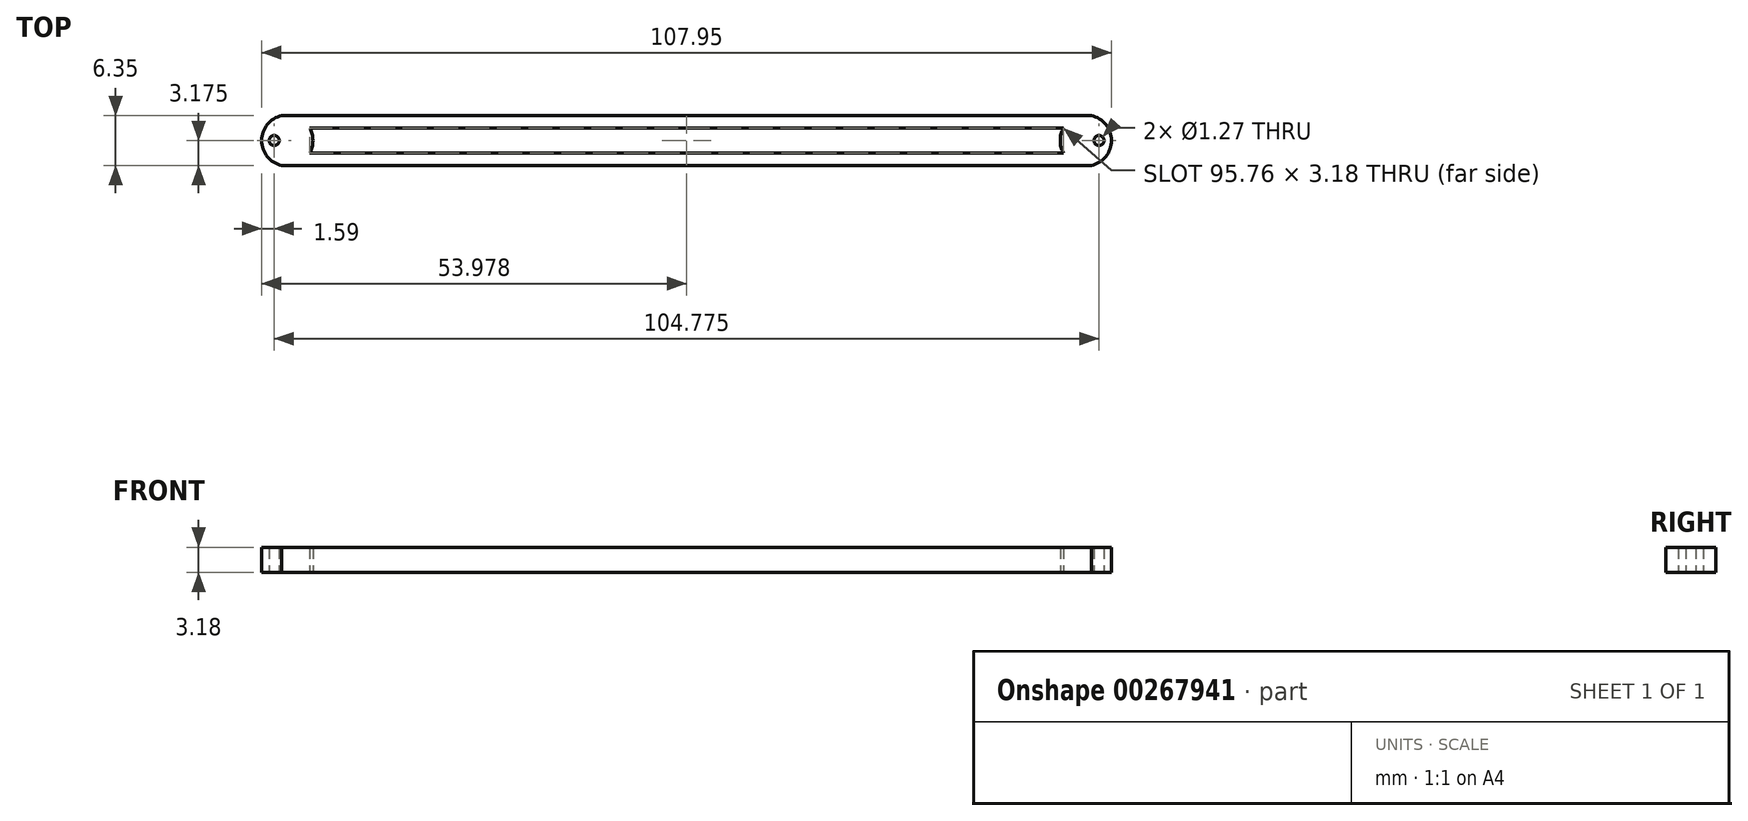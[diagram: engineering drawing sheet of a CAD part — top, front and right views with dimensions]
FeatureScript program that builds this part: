
annotation { "Feature Type Name" : "Feature", "Feature Type Description" : "" }
export const myFeature = defineFeature(function(context is Context, id is Id, definition is map)
    precondition{}
    {
        {
            var Q0;
            Q0=qCreatedBy(makeId("Top.planeOp"),FACE);
            var sketch = newSketch(context, id + "F0", { "sketchPlane" : qUnion([Q0])});
            skCircle(sketch, "E0", {"center": v(0, 0) * mm, "radius": 6.35 * mm, "construction": true});
            skLineSegment(sketch, "E1", {"start": v(0, -6.35) * mm, "end": v(0, 6.35) * mm, "construction": true});
            skArc(sketch, "E2", {"start": v(0, 6.35) * mm, "mid": v(-1.07, 8.92) * mm, "end": v(-3.64, 10) * mm, "construction": true});
            skLineSegment(sketch, "E3", {"start": v(-95.25, 0) * mm, "end": v(6.35, 0) * mm, "construction": true});
            skArc(sketch, "E4.MirrorCS", {"start": v(0, -6.35) * mm, "mid": v(-1.07, -8.92) * mm, "end": v(-3.64, -10) * mm, "construction": true});
            skLineSegment(sketch, "E5", {"start": v(-3.64, 10) * mm, "end": v(-3.64, 5.2) * mm, "construction": true});
            skLineSegment(sketch, "E6", {"start": v(-3.64, -10) * mm, "end": v(-3.64, -5.2) * mm, "construction": true});
            skArc(sketch, "E7", {"start": v(-8.34, 6.35) * mm, "mid": v(-5.99, 3.96) * mm, "end": v(-3.64, 6.35) * mm, "construction": true});
            skArc(sketch, "E8.MirrorCS", {"start": v(-8.34, -6.35) * mm, "mid": v(-5.99, -3.96) * mm, "end": v(-3.64, -6.35) * mm, "construction": true});
            skLineSegment(sketch, "E9", {"start": v(-95.25, 0) * mm, "end": v(-71.55, 6.35) * mm, "construction": true});
            skLineSegment(sketch, "E10", {"start": v(-8.34, 6.35) * mm, "end": v(-71.55, 6.35) * mm, "construction": true});
            skFitSpline(sketch, "E11", {"points": [v(-95.25, 0) * mm, v(-68.28, -8.17) * mm, v(-44.48, -8.52) * mm, v(-8.34, -6.35) * mm], "startDerivative": vector(42.5, -47.89) * mm, "endDerivative": vector(100.7, -12.48) * mm, "construction": true});
            skLineSegment(sketch, "E12", {"start": v(-95.25, 0) * mm, "end": v(-59.24, 6.35) * mm, "construction": true});
            skLineSegment(sketch, "E13", {"start": v(-3.64, 5.2) * mm, "end": v(-3.64, -0.24) * mm, "construction": true});
            skLineSegment(sketch, "E14", {"start": v(-3.64, -0.24) * mm, "end": v(-3.64, -5.2) * mm, "construction": true});
            skLineSegment(sketch, "E15.MirrorCS", {"start": v(3.64, 5.2) * mm, "end": v(3.64, -0.24) * mm, "construction": true});
            skLineSegment(sketch, "E16.MirrorCS", {"start": v(3.64, -0.24) * mm, "end": v(3.64, -5.2) * mm, "construction": true});
            skCircle(sketch, "E17", {"center": v(-3.64, -0.24) * mm, "radius": 0.64 * mm, "construction": true});
            skCircle(sketch, "E18", {"center": v(3.64, -0.24) * mm, "radius": 0.64 * mm, "construction": true});
            skLineSegment(sketch, "E19", {"start": v(0, 0) * mm, "end": v(0, 6.35) * mm, "construction": true});
            skLineSegment(sketch, "E20", {"start": v(0, 0) * mm, "end": v(0, -6.35) * mm, "construction": true});
            skCircle(sketch, "E21", {"center": v(0, -3.18) * mm, "radius": 0.64 * mm, "construction": true});
            skCircle(sketch, "E22", {"center": v(0, 3.18) * mm, "radius": 0.64 * mm, "construction": true});
            skFitSpline(sketch, "E23", {"points": [v(-1.07, 8.92) * mm, v(3.64, 5.2) * mm], "startDerivative": vector(3.04, -6.1) * mm, "endDerivative": vector(5.07, -1.86) * mm, "construction": true});
            skFitSpline(sketch, "E24.MirrorCS", {"points": [v(-1.07, -8.92) * mm, v(3.64, -5.2) * mm], "startDerivative": vector(3.04, 6.1) * mm, "endDerivative": vector(5.07, 1.86) * mm, "construction": true});
            skSolve(sketch);
        }
        {
            var Q0;
            Q0=qCreatedBy(makeId("Top.planeOp"),FACE);
            var sketch = newSketch(context, id + "F1", { "sketchPlane" : qUnion([Q0])});
            skLineSegment(sketch, "E25.bottom", {"start": v(-1.59, 4.76) * mm, "end": v(106.36, 4.76) * mm});
            skLineSegment(sketch, "E25.top", {"start": v(-1.59, 1.59) * mm, "end": v(106.36, 1.59) * mm});
            skLineSegment(sketch, "E25.left", {"start": v(-1.59, 4.76) * mm, "end": v(-1.59, 1.59) * mm});
            skLineSegment(sketch, "E25.right", {"start": v(106.36, 4.76) * mm, "end": v(106.36, 1.59) * mm});
            skLineSegment(sketch, "E26.top", {"start": v(0.95, 0) * mm, "end": v(103.82, 0) * mm});
            skLineSegment(sketch, "E26.left", {"start": v(-1.59, 2.54) * mm, "end": v(-1.59, 1.59) * mm});
            skLineSegment(sketch, "E26.right", {"start": v(106.36, 2.54) * mm, "end": v(106.36, 1.59) * mm});
            skLineSegment(sketch, "E27.top", {"start": v(0.95, 6.35) * mm, "end": v(103.82, 6.35) * mm});
            skLineSegment(sketch, "E27.left", {"start": v(-1.59, 3.8) * mm, "end": v(-1.59, 4.76) * mm});
            skLineSegment(sketch, "E27.right", {"start": v(106.36, 3.81) * mm, "end": v(106.36, 4.76) * mm});
            skCircle(sketch, "E28", {"center": v(0, 3.18) * mm, "radius": 0.64 * mm});
            skPoint(sketch, "E29.visualSharp", {"position": v(-1.59, 6.35) * mm});
            skArc(sketch, "E29.filletArc", {"start": v(0.95, 6.35) * mm, "mid": v(-0.84, 5.6) * mm, "end": v(-1.59, 3.8) * mm});
            skPoint(sketch, "E30.visualSharp", {"position": v(-1.59, 0) * mm});
            skArc(sketch, "E30.filletArc", {"start": v(-1.59, 2.54) * mm, "mid": v(-0.84, 0.74) * mm, "end": v(0.95, 0) * mm});
            skPoint(sketch, "E31.visualSharp", {"position": v(106.36, 6.35) * mm});
            skArc(sketch, "E31.filletArc", {"start": v(106.36, 3.81) * mm, "mid": v(105.62, 5.6) * mm, "end": v(103.82, 6.35) * mm});
            skPoint(sketch, "E32.visualSharp", {"position": v(106.36, 0) * mm});
            skArc(sketch, "E32.filletArc", {"start": v(103.82, 0) * mm, "mid": v(105.62, 0.74) * mm, "end": v(106.36, 2.54) * mm});
            skLineSegment(sketch, "E33", {"start": v(-1.59, 3.18) * mm, "end": v(106.36, 3.18) * mm, "construction": true});
            skCircle(sketch, "E34", {"center": v(104.77, 3.18) * mm, "radius": 0.64 * mm});
            skCircle(sketch, "E35", {"center": v(1.67, 3.18) * mm, "radius": 3.25 * mm});
            skLineSegment(sketch, "E36", {"start": v(52.39, 6.35) * mm, "end": v(52.39, 0) * mm, "construction": true});
            skCircle(sketch, "E37.MirrorC", {"center": v(103.1, 3.18) * mm, "radius": 3.25 * mm});
            skSolve(sketch);
        }
        {
            var Q0;
            {var subQ0=sQuery(id+"F1.wireOp",EDGE,"E35");var subQ1=sQuery(id+"F1.wireOp",EDGE,"E25.bottom");var subQ2=makeQuery(id+"F1.imprint","INTERSECT",VERTEX,{"disambiguationData":[OD(0.0)],"derivedFrom":[subQ1,subQ0]});Q0=makeQuery(id+"F1.imprint","IMPRINT",FACE,{"disambiguationData":[TD([[makeQuery(id+"F1.imprint","IMPRINT",EDGE,{"disambiguationData":[TD([[subQ2,-1.0]])],"derivedFrom":subQ1}),1.0]])]});}
            var Q1;
            Q1=makeQuery(id+"F1.imprint","IMPRINT",FACE,{"disambiguationData":[TD([[makeQuery(id+"F1.imprint","IMPRINT",EDGE,{"derivedFrom":sQuery(id+"F1.wireOp",EDGE,"E28")}),-1.0]])]});
            var Q2;
            {var subQ0=sQuery(id+"F1.wireOp",EDGE,"E35");var subQ1=sQuery(id+"F1.wireOp",EDGE,"E25.top");var subQ2=makeQuery(id+"F1.imprint","INTERSECT",VERTEX,{"disambiguationData":[OD(0.0)],"derivedFrom":[subQ1,subQ0]});Q2=makeQuery(id+"F1.imprint","IMPRINT",FACE,{"disambiguationData":[TD([[makeQuery(id+"F1.imprint","IMPRINT",EDGE,{"disambiguationData":[TD([[subQ2,-1.0]])],"derivedFrom":subQ1}),-1.0]])]});}
            var Q3;
            {var subQ0=sQuery(id+"F1.wireOp",EDGE,"E35");var subQ1=sQuery(id+"F1.wireOp",EDGE,"E25.top");var subQ2=makeQuery(id+"F1.imprint","INTERSECT",VERTEX,{"disambiguationData":[OD(1.0)],"derivedFrom":[subQ1,subQ0]});Q3=makeQuery(id+"F1.imprint","IMPRINT",FACE,{"disambiguationData":[TD([[makeQuery(id+"F1.imprint","IMPRINT",EDGE,{"disambiguationData":[TD([[subQ2,-1.0]])],"derivedFrom":subQ1}),-1.0]])]});}
            var Q4;
            {var subQ0=sQuery(id+"F1.wireOp",EDGE,"E35");var subQ1=sQuery(id+"F1.wireOp",EDGE,"E25.bottom");var subQ2=makeQuery(id+"F1.imprint","INTERSECT",VERTEX,{"disambiguationData":[OD(1.0)],"derivedFrom":[subQ1,subQ0]});Q4=makeQuery(id+"F1.imprint","IMPRINT",FACE,{"disambiguationData":[TD([[makeQuery(id+"F1.imprint","IMPRINT",EDGE,{"disambiguationData":[TD([[subQ2,-1.0]])],"derivedFrom":subQ1}),1.0]])]});}
            var Q5;
            {var subQ0=sQuery(id+"F1.wireOp",EDGE,"E35");var subQ1=sQuery(id+"F1.wireOp",EDGE,"E25.top");var subQ2=makeQuery(id+"F1.imprint","INTERSECT",VERTEX,{"disambiguationData":[OD(1.0)],"derivedFrom":[subQ1,subQ0]});Q5=makeQuery(id+"F1.imprint","IMPRINT",FACE,{"disambiguationData":[TD([[makeQuery(id+"F1.imprint","IMPRINT",EDGE,{"disambiguationData":[TD([[subQ2,-1.0]])],"derivedFrom":subQ1}),1.0]])]});}
            var Q6;
            {var subQ0=sQuery(id+"F1.wireOp",EDGE,"E37.MirrorC");var subQ1=sQuery(id+"F1.wireOp",EDGE,"E25.bottom");var subQ2=makeQuery(id+"F1.imprint","INTERSECT",VERTEX,{"disambiguationData":[OD(0.0)],"derivedFrom":[subQ1,subQ0]});Q6=makeQuery(id+"F1.imprint","IMPRINT",FACE,{"disambiguationData":[TD([[makeQuery(id+"F1.imprint","IMPRINT",EDGE,{"disambiguationData":[TD([[subQ2,-1.0]])],"derivedFrom":subQ1}),1.0]])]});}
            var Q7;
            Q7=makeQuery(id+"F1.imprint","IMPRINT",FACE,{"disambiguationData":[TD([[makeQuery(id+"F1.imprint","IMPRINT",EDGE,{"derivedFrom":sQuery(id+"F1.wireOp",EDGE,"E34")}),-1.0]])]});
            var Q8;
            {var subQ0=sQuery(id+"F1.wireOp",EDGE,"E37.MirrorC");var subQ1=sQuery(id+"F1.wireOp",EDGE,"E25.top");var subQ2=makeQuery(id+"F1.imprint","INTERSECT",VERTEX,{"disambiguationData":[OD(0.0)],"derivedFrom":[subQ1,subQ0]});Q8=makeQuery(id+"F1.imprint","IMPRINT",FACE,{"disambiguationData":[TD([[makeQuery(id+"F1.imprint","IMPRINT",EDGE,{"disambiguationData":[TD([[subQ2,-1.0]])],"derivedFrom":subQ1}),-1.0]])]});}
            extrude(context, id + "F2", {"entities" : qUnion([Q0, Q1, Q2, Q3, Q4, Q5, Q6, Q7, Q8]), "depth" : 3.17 * mm, "offsetDistance" : 25.4 * mm});
        }
    });
